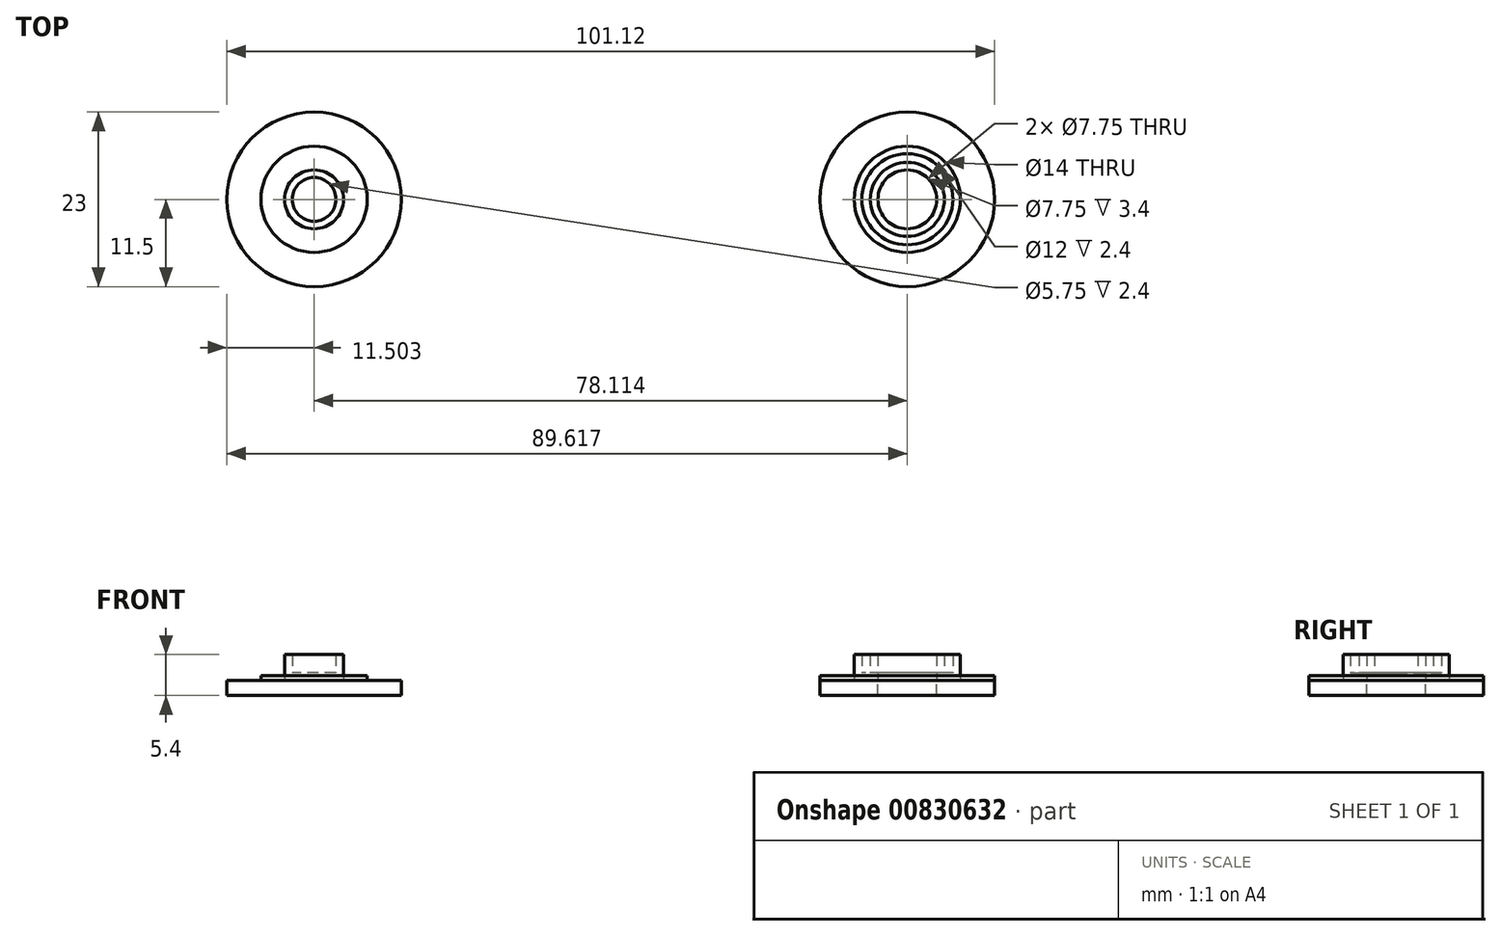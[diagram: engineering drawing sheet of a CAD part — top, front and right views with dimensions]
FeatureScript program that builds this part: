
annotation { "Feature Type Name" : "Feature", "Feature Type Description" : "" }
export const myFeature = defineFeature(function(context is Context, id is Id, definition is map)
    precondition{}
    {
        {
            var Q0;
            Q0=qCreatedBy(makeId("Top.planeOp"),FACE);
            var sketch = newSketch(context, id + "F0", { "sketchPlane" : qUnion([Q0])});
            skCircle(sketch, "E0", {"center": v(-39.06, 0) * mm, "radius": 3.88 * mm});
            skCircle(sketch, "E1", {"center": v(-39.06, 0) * mm, "radius": 7 * mm});
            skCircle(sketch, "E2", {"center": v(-39.06, 0) * mm, "radius": 11.5 * mm});
            skCircle(sketch, "E3.MirrorC", {"center": v(39.06, 0) * mm, "radius": 11.5 * mm});
            skCircle(sketch, "E4.MirrorC", {"center": v(39.06, 0) * mm, "radius": 7 * mm});
            skCircle(sketch, "E5.MirrorC", {"center": v(39.06, 0) * mm, "radius": 3.88 * mm});
            skSolve(sketch);
        }
        {
            var Q0;
            Q0=makeQuery(id+"F0.imprint","IMPRINT",FACE,{"disambiguationData":[TD([[makeQuery(id+"F0.imprint","IMPRINT",EDGE,{"derivedFrom":sQuery(id+"F0.wireOp",EDGE,"E0")}),1.0]])]});
            var Q1;
            Q1=makeQuery(id+"F0.imprint","IMPRINT",FACE,{"disambiguationData":[TD([[makeQuery(id+"F0.imprint","IMPRINT",EDGE,{"derivedFrom":sQuery(id+"F0.wireOp",EDGE,"E5.MirrorC")}),-1.0]])]});
            extrude(context, id + "F1", {"entities" : qUnion([Q0, Q1]), "depth" : 3.4 * mm, "offsetDistance" : 25 * mm});
        }
        {
            var Q0;
            Q0=makeQuery(id+"F0.imprint","IMPRINT",FACE,{"disambiguationData":[TD([[makeQuery(id+"F0.imprint","IMPRINT",EDGE,{"derivedFrom":sQuery(id+"F0.wireOp",EDGE,"E0")}),-1.0]])]});
            var Q1;
            Q1=makeQuery(id+"F0.imprint","IMPRINT",FACE,{"disambiguationData":[TD([[makeQuery(id+"F0.imprint","IMPRINT",EDGE,{"derivedFrom":sQuery(id+"F0.wireOp",EDGE,"E4.MirrorC")}),-1.0]])]});
            extrude(context, id + "F2", {"entities" : qUnion([Q0, Q1]), "depth" : 0.6 * mm, "offsetDistance" : 25 * mm});
        }
        {
            var Q0;
            Q0=makeQuery(id+"F0.imprint","IMPRINT",FACE,{"disambiguationData":[TD([[makeQuery(id+"F0.imprint","IMPRINT",EDGE,{"derivedFrom":sQuery(id+"F0.wireOp",EDGE,"E1")}),-1.0]])]});
            var Q1;
            Q1=makeQuery(id+"F0.imprint","IMPRINT",FACE,{"disambiguationData":[TD([[makeQuery(id+"F0.imprint","IMPRINT",EDGE,{"derivedFrom":sQuery(id+"F0.wireOp",EDGE,"E3.MirrorC")}),-1.0]])]});
            var Q2;
            Q2=makeQuery(id+"F0.imprint","IMPRINT",FACE,{"disambiguationData":[TD([[makeQuery(id+"F0.imprint","IMPRINT",EDGE,{"derivedFrom":sQuery(id+"F0.wireOp",EDGE,"E0")}),-1.0]])]});
            var Q3;
            Q3=makeQuery(id+"F0.imprint","IMPRINT",FACE,{"disambiguationData":[TD([[makeQuery(id+"F0.imprint","IMPRINT",EDGE,{"derivedFrom":sQuery(id+"F0.wireOp",EDGE,"E0")}),1.0]])]});
            var Q4;
            Q4=makeQuery(id+"F0.imprint","IMPRINT",FACE,{"disambiguationData":[TD([[makeQuery(id+"F0.imprint","IMPRINT",EDGE,{"derivedFrom":sQuery(id+"F0.wireOp",EDGE,"E4.MirrorC")}),-1.0]])]});
            var Q5;
            Q5=makeQuery(id+"F0.imprint","IMPRINT",FACE,{"disambiguationData":[TD([[makeQuery(id+"F0.imprint","IMPRINT",EDGE,{"derivedFrom":sQuery(id+"F0.wireOp",EDGE,"E5.MirrorC")}),-1.0]])]});
            extrude(context, id + "F3", {"entities" : qUnion([Q0, Q1, Q2, Q3, Q4, Q5]), "oppositeDirection" : true, "depth" : 2 * mm, "offsetDistance" : 25 * mm});
        }
        {
            var Q0;
            Q0=makeQuery(id+"F1.opExtrude","CAP_FACE",FACE,{"disambiguationData":[OSD([sQuery(id+"F0.wireOp",EDGE,"E0")])],"isStart":false});
            var Q1;
            Q1=makeQuery(id+"F1.opExtrude","CAP_FACE",FACE,{"disambiguationData":[OSD([sQuery(id+"F0.wireOp",EDGE,"E5.MirrorC")])],"isStart":false});
            shell(context, id + "F4", {"entities" : qUnion([Q0, Q1]), "thickness" : 1 * mm});
        }
    });
